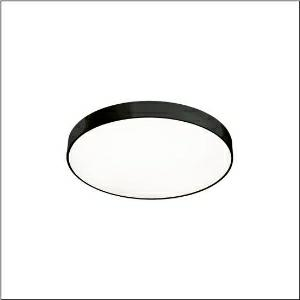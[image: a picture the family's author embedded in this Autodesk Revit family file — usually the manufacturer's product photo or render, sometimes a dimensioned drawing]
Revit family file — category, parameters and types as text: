
# Revit family: round_21_m_51mr36gd0421b
name_source: partatom
category: Lighting Fixtures
units: mm (PartAtom-declared; Revit-internal decimal feet)

## family parameters
Cut with Voids When Loaded = No
Host = Face
Light Source = No
Part Type = Normal
Room Calculation Point = No
Round Connector Dimension = Use Diameter
Shared = No

## types (1)
- Round 21 M (1 x LED, 7870 lm, 54.6 W, 4000K)
    Apparent Load = 55 VA
    CIE Flux Codes = 49 80 96 85 100
    Color Rendering = 80
    Color Temperature = 4000K
    Default Elevation = 1800 mm
    Description = Round 21 M, wall and ceiling luminaire, primary optical cover: cover, of PMMA, opal, light emission: direct/indirect distribution, primary light characteristic: symmetric, installation type: suspended mounting, surface-mounted, LED, rated luminous flux: 7.870lm, luminous efficacy: 144lm/W, light colour: 840, colour temperature: 4000K, control gear: DALI 2, with terminal, 5-pole, mains connection: 230V, AC, 50/60Hz, rated input power: 54.6W, housing, of aluminium, coated, black, diameter: 600mm, height: 62mm, protection rating (complete): IP40, insulation class (complete): insulation class I (protective earthing), certification: CE, impact resistance: IK04, permissible operating ambient temperature: -10..+35°C, packaging unit: 1 piece
    Height = 87 mm
    Lamp = 1 x LED
    Lamp Light Flux = 7870 lm
    Lamp Power = 54.6 W
    Lamp count = 1
    Length = 600 mm
    Luminous efficacy = 144 lm/W
    Manufacturer = Siteco
    ModVariant = No
    Model = 51MR36GD0421B
    Mounting Place = Ceiling
    Mounting Type = Surface mounted
    Number of Poles = 1
    OnlyDefault = Yes
    Power Factor = 1
    Product Name = Round 21 M
    Product group = wall and ceiling luminaire
    ProductGroupID = 304
    Protection Class = Protection class I
    Protection Degree = IP 40
    RLX_Detail_Level = 1
    RLX_Emergency_Light_Flux = 0 lm
    RLX_Emergency_Type = 0
    RLX_Emergency_Type_DB = No
    RlxData = <blob elided: 18141 chars, md5=66f026c7>
    Socket = socket
    Standby Power = 0 W
    System Light Flux = 7870 lm
    System Power = 55 W
    Type Comments = Product without accessories
    Type Image = l_1258332.jpg
    URL = http://relux.com
    VarID = ---
    Voltage = 0 V
    Weight = 0.00 kg
    Width = 0 mm  [stored 0 ft]

note: [stored X ft] marks values corroborated as IEEE doubles in the binary element streams (Revit-internal decimal feet)

## geometry (parser evidence)
native form markers: Blend x4, Sweep x13
no freeform markers — native parametric forms only
